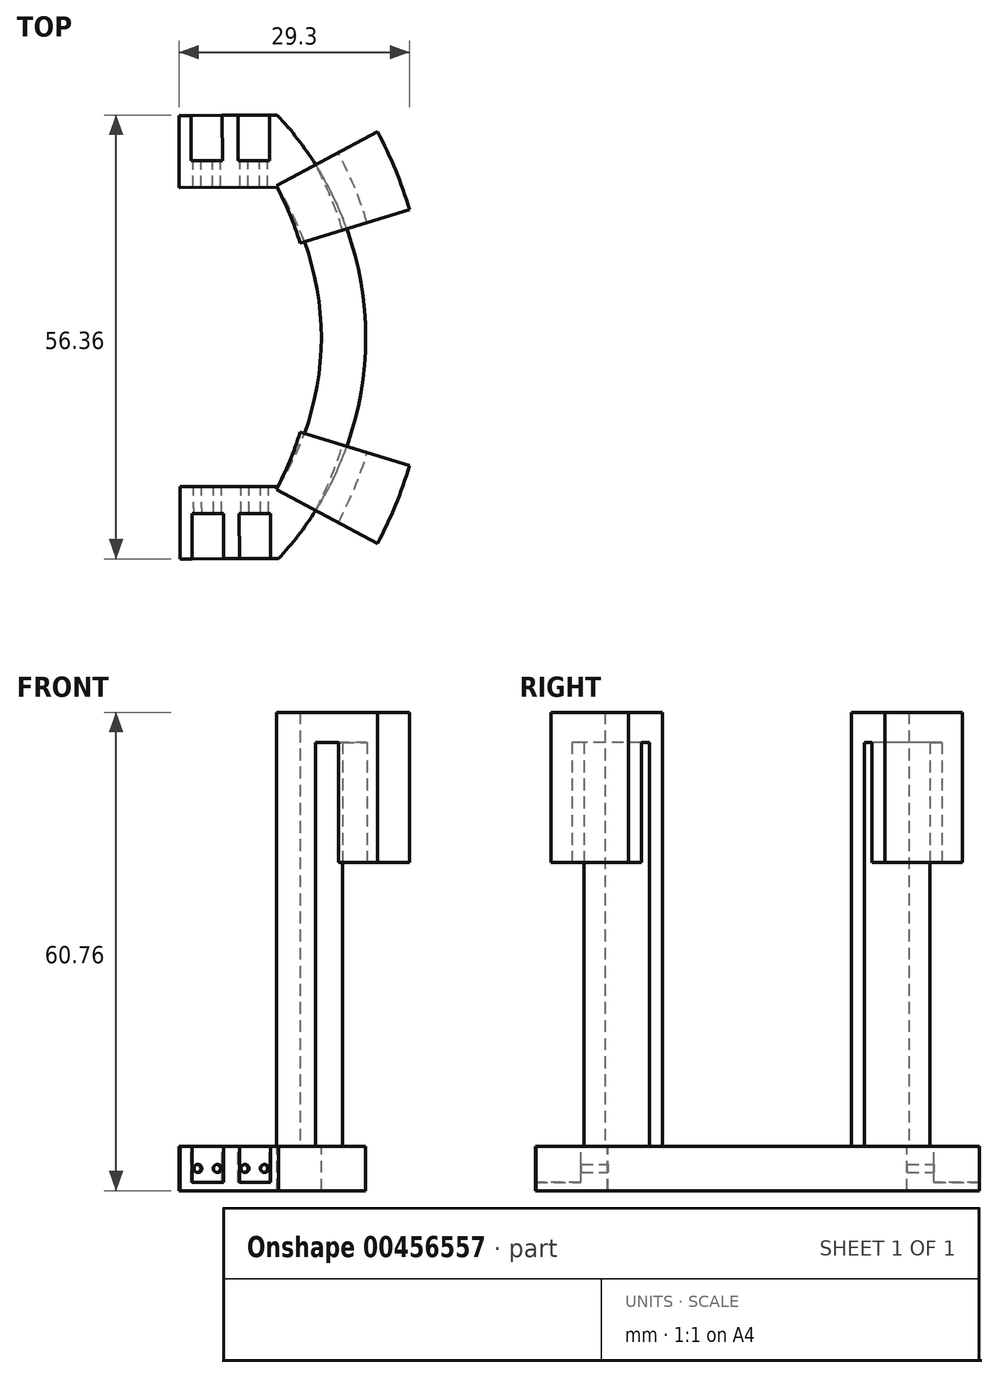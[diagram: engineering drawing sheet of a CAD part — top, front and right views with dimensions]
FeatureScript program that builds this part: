
annotation { "Feature Type Name" : "Feature", "Feature Type Description" : "" }
export const myFeature = defineFeature(function(context is Context, id is Id, definition is map)
    precondition{}
    {
        {
            var Q0;
            Q0=qCreatedBy(makeId("Front.planeOp"),FACE);
            var sketch = newSketch(context, id + "F0", { "sketchPlane" : qUnion([Q0])});
            skLineSegment(sketch, "E0", {"start": v(0, 51.3) * mm, "end": v(3.28, 51.3) * mm});
            skLineSegment(sketch, "E1", {"start": v(3.28, 51.3) * mm, "end": v(3.28, 36.07) * mm});
            skLineSegment(sketch, "E2", {"start": v(3.28, 36.07) * mm, "end": v(8.92, 36.07) * mm});
            skLineSegment(sketch, "E3", {"start": v(8.92, 36.07) * mm, "end": v(8.92, 55.12) * mm});
            skLineSegment(sketch, "E4", {"start": v(8.92, 55.12) * mm, "end": v(-5.64, 55.12) * mm});
            skLineSegment(sketch, "E5", {"start": v(-5.64, 55.12) * mm, "end": v(-5.64, 0) * mm});
            skLineSegment(sketch, "E6", {"start": v(0, 51.3) * mm, "end": v(0, 0) * mm});
            skLineSegment(sketch, "E7", {"start": v(-5.64, 0) * mm, "end": v(0, 0) * mm});
            skLineSegment(sketch, "E8", {"start": v(-5.64, 0) * mm, "end": v(-46.76, 0) * mm, "construction": true});
            skLineSegment(sketch, "E9", {"start": v(-46.76, 0) * mm, "end": v(-46.76, 40.72) * mm, "construction": true});
            skSolve(sketch);
        }
        {
            var Q0;
            Q0=makeQuery(id+"F0.imprint","IMPRINT",FACE,{"disambiguationData":[TD([[makeQuery(id+"F0.imprint","IMPRINT",EDGE,{"derivedFrom":sQuery(id+"F0.wireOp",EDGE,"E0")}),1.0]])]});
            var Q1;
            Q1=sQuery(id+"F0.wireOp",EDGE,"E9");
            revolve(context, id + "F1", {"entities" : qUnion([Q0]), "axis" : qUnion([Q1]), "revolveType" : RevolveType.SYMMETRIC, "angle" : 56 * degree});
        }
        {
            var Q0;
            Q0 = qSketchRegion(id + "F0", true);
            var Q1;
            Q1=sQuery(id+"F0.wireOp",EDGE,"E9");
            revolve(context, id + "F2", {"operationType" : NewBodyOperationType.REMOVE, "entities" : qUnion([Q0]), "axis" : qUnion([Q1]), "revolveType" : RevolveType.SYMMETRIC, "oppositeDirection" : true, "angle" : 34 * degree});
        }
        {
            var Q0;
            Q0=qCreatedBy(makeId("Top.planeOp"),FACE);
            var sketch = newSketch(context, id + "F3", { "sketchPlane" : qUnion([Q0])});
            skArc(sketch, "E10", {"start": v(-10.17, -28.08) * mm, "mid": v(0.9, 0.12) * mm, "end": v(-10.33, 28.25) * mm});
            skLineSegment(sketch, "E11", {"start": v(-10.33, 28.25) * mm, "end": v(-10.3, 19.09) * mm, "construction": true});
            skArc(sketch, "E12", {"start": v(-10.2, -18.91) * mm, "mid": v(-4.74, 0.1) * mm, "end": v(-10.3, 19.09) * mm});
            skLineSegment(sketch, "E13", {"start": v(-10.33, 28.25) * mm, "end": v(-22.82, 28.21) * mm});
            skLineSegment(sketch, "E14", {"start": v(-22.82, 28.21) * mm, "end": v(-22.8, 19.05) * mm});
            skLineSegment(sketch, "E15.trimOffspring", {"start": v(-10.2, -18.91) * mm, "end": v(-10.17, -28.08) * mm, "construction": true});
            skLineSegment(sketch, "E16", {"start": v(-22.8, 19.05) * mm, "end": v(-10.3, 19.09) * mm});
            skLineSegment(sketch, "E17", {"start": v(-10.2, -18.91) * mm, "end": v(-22.69, -18.95) * mm});
            skLineSegment(sketch, "E18", {"start": v(-22.69, -18.95) * mm, "end": v(-22.66, -28.11) * mm});
            skLineSegment(sketch, "E19", {"start": v(-22.66, -28.11) * mm, "end": v(-10.17, -28.08) * mm});
            skSolve(sketch);
        }
        {
            var Q0;
            Q0 = qSketchRegion(id + "F3", true);
            extrude(context, id + "F4", {"entities" : qUnion([Q0]), "operationType" : NewBodyOperationType.ADD, "oppositeDirection" : true, "depth" : 5.64 * mm, "offsetDistance" : 25.4 * mm});
        }
        {
            var Q0;
            Q0=makeQuery(id+"F4.opExtrude","CAP_FACE",FACE,{"disambiguationData":[OSD([sQuery(id+"F3.wireOp",EDGE,"E10"),sQuery(id+"F3.wireOp",EDGE,"E12"),sQuery(id+"F3.wireOp",EDGE,"E13"),sQuery(id+"F3.wireOp",EDGE,"E14"),sQuery(id+"F3.wireOp",EDGE,"E16"),sQuery(id+"F3.wireOp",EDGE,"E17"),sQuery(id+"F3.wireOp",EDGE,"E18"),sQuery(id+"F3.wireOp",EDGE,"E19")])],"isStart":true});
            var sketch = newSketch(context, id + "F5", { "sketchPlane" : qUnion([Q0])});
            skLineSegment(sketch, "E20", {"start": v(-21.14, -28.1) * mm, "end": v(-21.16, -22.36) * mm});
            skLineSegment(sketch, "E21", {"start": v(-21.16, -22.36) * mm, "end": v(-17.17, -22.35) * mm});
            skLineSegment(sketch, "E22", {"start": v(-17.17, -22.35) * mm, "end": v(-17.15, -28.1) * mm});
            skLineSegment(sketch, "E23", {"start": v(-15.15, -28.1) * mm, "end": v(-15.16, -22.35) * mm});
            skLineSegment(sketch, "E24", {"start": v(-15.16, -22.35) * mm, "end": v(-11.17, -22.34) * mm});
            skLineSegment(sketch, "E25", {"start": v(-11.17, -22.34) * mm, "end": v(-11.16, -28.08) * mm});
            skLineSegment(sketch, "E26", {"start": v(-21.3, 28.22) * mm, "end": v(-21.28, 22.47) * mm});
            skLineSegment(sketch, "E27", {"start": v(-21.28, 22.47) * mm, "end": v(-17.3, 22.48) * mm});
            skLineSegment(sketch, "E28", {"start": v(-17.3, 22.48) * mm, "end": v(-17.31, 28.25) * mm});
            skLineSegment(sketch, "E29", {"start": v(-15.3, 28.24) * mm, "end": v(-15.29, 22.48) * mm});
            skLineSegment(sketch, "E30", {"start": v(-15.29, 22.48) * mm, "end": v(-11.3, 22.5) * mm});
            skLineSegment(sketch, "E31", {"start": v(-17.3, 22.48) * mm, "end": v(-17.17, -22.35) * mm, "construction": true});
            skLineSegment(sketch, "E32", {"start": v(-11.32, 28.25) * mm, "end": v(-11.3, 22.5) * mm});
            skSolve(sketch);
        }
        {
            var Q0;
            {var subQ0=sQuery(id+"F5.wireOp",EDGE,"E20");Q0=makeQuery(id+"F5.imprint","IMPRINT",FACE,{"disambiguationData":[TD([[makeQuery(id+"F5.imprint","IMPRINT",EDGE,{"derivedFrom":subQ0}),-1.0]])]});}
            var Q1;
            {var subQ0=sQuery(id+"F5.wireOp",EDGE,"E23");Q1=makeQuery(id+"F5.imprint","IMPRINT",FACE,{"disambiguationData":[TD([[makeQuery(id+"F5.imprint","IMPRINT",EDGE,{"derivedFrom":subQ0}),-1.0]])]});}
            var Q2;
            {var subQ0=sQuery(id+"F5.wireOp",EDGE,"E26");Q2=makeQuery(id+"F5.imprint","IMPRINT",FACE,{"disambiguationData":[TD([[makeQuery(id+"F5.imprint","IMPRINT",EDGE,{"derivedFrom":subQ0}),1.0]])]});}
            var Q3;
            {var subQ0=sQuery(id+"F5.wireOp",EDGE,"E29");Q3=makeQuery(id+"F5.imprint","IMPRINT",FACE,{"disambiguationData":[TD([[makeQuery(id+"F5.imprint","IMPRINT",EDGE,{"derivedFrom":subQ0}),1.0]])]});}
            var Q4;
            Q4 = qConstructionFilter(qBodyType(qCreatedBy(id + "F5" ,EDGE), BodyType.WIRE), ConstructionObject.NO);
            extrude(context, id + "F6", {"entities" : qUnion([Q0, Q1, Q2, Q3]), "operationType" : NewBodyOperationType.REMOVE, "surfaceEntities" : qUnion([Q4]), "oppositeDirection" : true, "depth" : 4.57 * mm, "offsetDistance" : 25.4 * mm});
        }
        {
            var Q0;
            Q0=makeQuery(id+"F6.boolean.opBoolean","COPY",FACE,{"derivedFrom":makeQuery(id+"F6.opExtrude","SWEPT_FACE",FACE,{"disambiguationData":[OSD([sQuery(id+"F5.wireOp",EDGE,"E30")])]})});
            var sketch = newSketch(context, id + "F7", { "sketchPlane" : qUnion([Q0])});
            skCircle(sketch, "E33", {"center": v(12, -2.82) * mm, "radius": 0.5 * mm});
            skCircle(sketch, "E34", {"center": v(14.49, -2.82) * mm, "radius": 0.5 * mm});
            skSolve(sketch);
        }
        {
            var Q0;
            Q0=makeQuery(id+"F7.imprint","IMPRINT",FACE,{"disambiguationData":[TD([[makeQuery(id+"F7.imprint","IMPRINT",EDGE,{"derivedFrom":sQuery(id+"F7.wireOp",EDGE,"E33")}),1.0]])]});
            var Q1;
            Q1=makeQuery(id+"F7.imprint","IMPRINT",FACE,{"disambiguationData":[TD([[makeQuery(id+"F7.imprint","IMPRINT",EDGE,{"derivedFrom":sQuery(id+"F7.wireOp",EDGE,"E34")}),1.0]])]});
            extrude(context, id + "F8", {"entities" : qUnion([Q0, Q1]), "operationType" : NewBodyOperationType.REMOVE, "oppositeDirection" : true, "depth" : 99.57 * mm, "offsetDistance" : 25.4 * mm});
        }
        {
            var Q0;
            Q0=makeQuery(id+"F6.boolean.opBoolean","COPY",FACE,{"derivedFrom":makeQuery(id+"F6.opExtrude","SWEPT_FACE",FACE,{"disambiguationData":[OSD([sQuery(id+"F5.wireOp",EDGE,"E27")])]})});
            var sketch = newSketch(context, id + "F9", { "sketchPlane" : qUnion([Q0])});
            skCircle(sketch, "E35", {"center": v(18, -2.82) * mm, "radius": 0.5 * mm});
            skCircle(sketch, "E36", {"center": v(20.48, -2.82) * mm, "radius": 0.5 * mm});
            skSolve(sketch);
        }
        {
            var Q0;
            Q0=makeQuery(id+"F9.imprint","IMPRINT",FACE,{"disambiguationData":[TD([[makeQuery(id+"F9.imprint","IMPRINT",EDGE,{"derivedFrom":sQuery(id+"F9.wireOp",EDGE,"E35")}),1.0]])]});
            var Q1;
            Q1=makeQuery(id+"F9.imprint","IMPRINT",FACE,{"disambiguationData":[TD([[makeQuery(id+"F9.imprint","IMPRINT",EDGE,{"derivedFrom":sQuery(id+"F9.wireOp",EDGE,"E36")}),1.0]])]});
            extrude(context, id + "F10", {"entities" : qUnion([Q0, Q1]), "operationType" : NewBodyOperationType.REMOVE, "oppositeDirection" : true, "depth" : 72.39 * mm, "offsetDistance" : 25.4 * mm});
        }
    });
